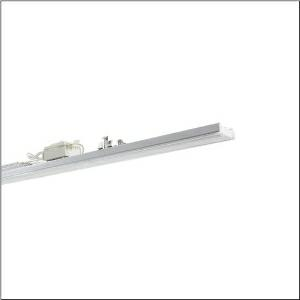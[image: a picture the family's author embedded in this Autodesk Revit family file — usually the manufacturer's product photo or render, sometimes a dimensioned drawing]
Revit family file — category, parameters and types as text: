
# Revit family: licross_r__21_recessed_mo_52te11dv4fxg_dcfe
name_source: partatom
category: Lighting Fixtures
units: mm (PartAtom-declared; Revit-internal decimal feet)

## family parameters
Cut with Voids When Loaded = No
Host = Face
Light Source = No
Part Type = Normal
Room Calculation Point = No
Round Connector Dimension = Use Diameter
Shared = No

## types (1)
- --- (1 x LED, 15180 lm, 85.3 W, 4000K)
    Apparent Load = 85 VA
    CIE Flux Codes = 89 96 99 100 100
    Color Rendering = 80
    Color Temperature = 4000K
    Default Elevation = 1800 mm
    Description = Licross® 21 Recessed MO, luminaire insert, of sheet steel, galvanised, coil coated, white, length: 2.250mm, width: 66mm, height: 67mm, LED rated luminous flux: 15.180lm, light colour: 840, control gear: DALI 2, with plug, 5-pole, with phase selection, mains connection: 220..240V, AC, 50/60Hz, rated input power: 85W, halogen-free wiring, primary light control with lens, of plastic, primary optical cover: cover, of PMMA, light emission: direct distribution, primary light characteristic: symmetric, protection rating (complete): IP54, insulation class (complete): insulation class I (protective earthing), certification: CE, ENEC, VDE, UKCA, protection symbol: D if used in an environment with non-conductive dust loads with corresponding accessories, impact resistance: IK06, permissible ambient temperature for indoor applications: -25..+35°C, corresponds to IFS (International Featured Standards) requirements for safety and quality in the food industry, reducing of maximum allowable ambient temperature of 5°C with ceiling mounting, LABS conformity tested according to VDMA 24364:2018-05, packaging unit: 1 piece
    Height = 58 mm
    Lamp = 1 x LED
    Lamp Light Flux = 15180 lm
    Lamp Power = 85.3 W
    Lamp count = 1
    Length = 2250 mm
    Luminous efficacy = 178 lm/W
    Manufacturer = Siteco
    ModVariant = No
    Model = 52TE11DV4FXG
    Mounting Place = Ceiling
    Mounting Type = Pendant
    Number of Poles = 1
    OnlyDefault = Yes
    Power Factor = 1
    Product Name = Licross® 21 Recessed MO
    Product group = luminaire insert
    ProductGroupID = 902
    Protection Class = Protection class I
    Protection Degree = IP 54
    RLX_Detail_Level = 1
    RLX_Emergency_Light_Flux = 0 lm
    RLX_Emergency_Type = 0
    RLX_Emergency_Type_DB = No
    RlxData = <blob elided: 29317 chars, md5=06008c0e>
    Socket = socket
    Standby Power = 0 W
    System Light Flux = 15180 lm
    System Power = 85 W
    Type Comments = factory setting: luminous flux: 100 % | dim-lin: 254 | 390 mA
    Type Image = l_1296930.jpg
    URL = http://relux.com
    VarID = @adj_127050
    Voltage = 0 V
    Weight = 0.00 kg
    Width = 66 mm

## geometry (parser evidence)
native form markers: Blend x4, Sweep x10
no freeform markers — native parametric forms only
